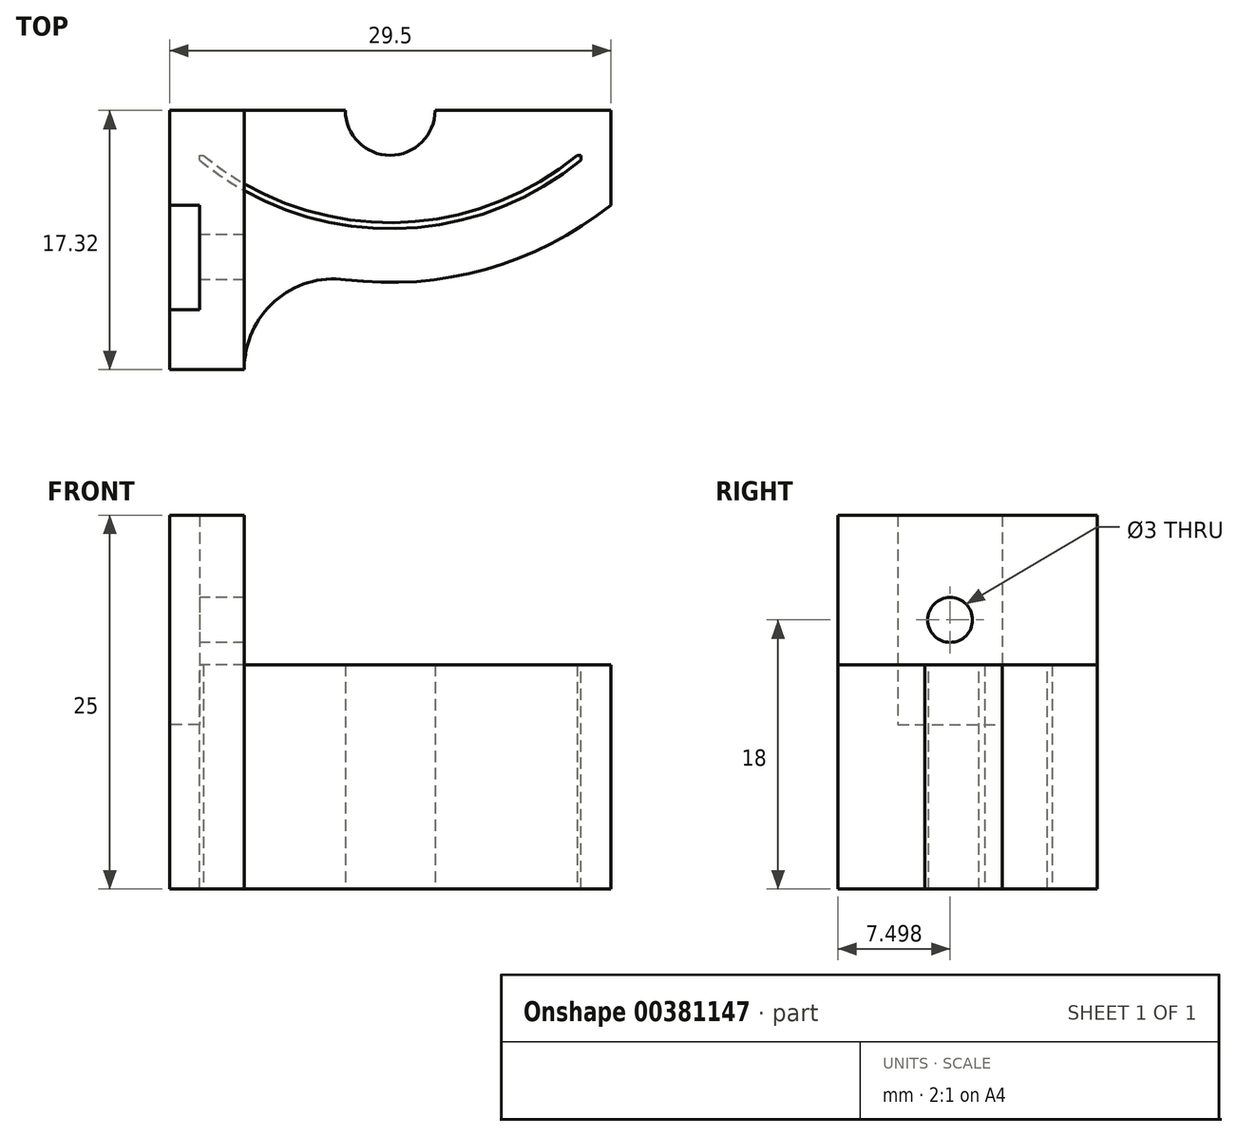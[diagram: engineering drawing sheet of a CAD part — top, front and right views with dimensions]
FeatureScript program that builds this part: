
annotation { "Feature Type Name" : "Feature", "Feature Type Description" : "" }
export const myFeature = defineFeature(function(context is Context, id is Id, definition is map)
    precondition{}
    {
        {
            var Q0;
            Q0=qCreatedBy(makeId("Top.planeOp"),FACE);
            var sketch = newSketch(context, id + "F0", { "sketchPlane" : qUnion([Q0])});
            skLineSegment(sketch, "E0", {"start": v(0, 0) * mm, "end": v(25, 0) * mm});
            skArc(sketch, "E1", {"start": v(0, 0) * mm, "mid": v(12.5, -4.5) * mm, "end": v(25, 0) * mm});
            skLineSegment(sketch, "E2.top", {"start": v(0, 3) * mm, "end": v(25, 3) * mm});
            skLineSegment(sketch, "E2.left", {"start": v(0, 0) * mm, "end": v(0, 3) * mm});
            skLineSegment(sketch, "E2.right", {"start": v(25, 0) * mm, "end": v(25, 3) * mm});
            skSolve(sketch);
        }
        {
            var Q0;
            Q0=makeQuery(id+"F0.imprint","IMPRINT",FACE,{"disambiguationData":[TD([[makeQuery(id+"F0.imprint","IMPRINT",EDGE,{"derivedFrom":sQuery(id+"F0.wireOp",EDGE,"E0")}),1.0]])]});
            var Q1;
            Q1=makeQuery(id+"F0.imprint","IMPRINT",FACE,{"disambiguationData":[TD([[makeQuery(id+"F0.imprint","IMPRINT",EDGE,{"derivedFrom":sQuery(id+"F0.wireOp",EDGE,"E1")}),1.0]])]});
            extrude(context, id + "F1", {"entities" : qUnion([Q0, Q1]), "depth" : 25 * mm});
        }
        {
            var Q0;
            Q0=makeQuery(id+"F1.opExtrude","CAP_FACE",FACE,{"disambiguationData":[OSD([sQuery(id+"F0.wireOp",EDGE,"E1"),sQuery(id+"F0.wireOp",EDGE,"E2.top"),sQuery(id+"F0.wireOp",EDGE,"E2.left"),sQuery(id+"F0.wireOp",EDGE,"E2.right")])],"isStart":false});
            var sketch = newSketch(context, id + "F2", { "sketchPlane" : qUnion([Q0])});
            skArc(sketch, "E3.0", {"start": v(-0.25, -0.3) * mm, "mid": v(12.5, -4.9) * mm, "end": v(25.25, -0.3) * mm});
            skLineSegment(sketch, "E4", {"start": v(-0.25, -0.3) * mm, "end": v(-2.25, -0.3) * mm});
            skLineSegment(sketch, "E5", {"start": v(-2.25, -0.3) * mm, "end": v(-2.25, 3) * mm});
            skLineSegment(sketch, "E6", {"start": v(0, 3) * mm, "end": v(-2.25, 3) * mm});
            skLineSegment(sketch, "E7", {"start": v(-0.25, -0.3) * mm, "end": v(-0.25, 0) * mm});
            skLineSegment(sketch, "E8", {"start": v(-0.25, 0) * mm, "end": v(0, 0) * mm});
            skArc(sketch, "E9.0", {"start": v(-2.25, -3.32) * mm, "mid": v(12.5, -8.5) * mm, "end": v(27.25, -3.32) * mm});
            skLineSegment(sketch, "E10", {"start": v(-2.25, -0.3) * mm, "end": v(-2.25, -3.32) * mm});
            skLineSegment(sketch, "E11.MirrorCS", {"start": v(25.25, 0) * mm, "end": v(25, 0) * mm});
            skLineSegment(sketch, "E12.MirrorCS", {"start": v(25.25, -0.3) * mm, "end": v(25.25, 0) * mm});
            skLineSegment(sketch, "E13.MirrorCS", {"start": v(25.25, -0.3) * mm, "end": v(27.25, -0.3) * mm});
            skLineSegment(sketch, "E14.MirrorCS", {"start": v(27.25, -0.3) * mm, "end": v(27.25, 3) * mm});
            skLineSegment(sketch, "E15.MirrorCS", {"start": v(27.25, -0.3) * mm, "end": v(27.25, -3.32) * mm});
            skLineSegment(sketch, "E16.MirrorCS", {"start": v(25, 3) * mm, "end": v(27.25, 3) * mm});
            skSolve(sketch);
        }
        {
            var Q0;
            Q0=makeQuery(id+"F2.imprint","IMPRINT",FACE,{"disambiguationData":[TD([[makeQuery(id+"F2.imprint","IMPRINT",EDGE,{"derivedFrom":sQuery(id+"F2.wireOp",EDGE,"E4")}),-1.0]])]});
            var Q1;
            Q1=makeQuery(id+"F2.imprint","IMPRINT",FACE,{"disambiguationData":[TD([[makeQuery(id+"F2.imprint","IMPRINT",EDGE,{"derivedFrom":sQuery(id+"F2.wireOp",EDGE,"E3.0")}),-1.0]])]});
            var Q2;
            Q2=makeQuery(id+"F2.imprint","IMPRINT",FACE,{"disambiguationData":[TD([[makeQuery(id+"F2.imprint","IMPRINT",EDGE,{"derivedFrom":sQuery(id+"F2.wireOp",EDGE,"E11.MirrorCS")}),-1.0]])]});
            extrude(context, id + "F3", {"entities" : qUnion([Q0, Q1, Q2]), "oppositeDirection" : true, "depth" : 25 * mm});
        }
        {
            var Q0;
            Q0=makeQuery(id+"F3.opExtrude","SWEPT_BODY",BODY,{"disambiguationData":[OSD([sQuery(id+"F0.wireOp",EDGE,"E2.left"),sQuery(id+"F0.wireOp",EDGE,"E2.right"),sQuery(id+"F2.wireOp",EDGE,"E3.0"),sQuery(id+"F2.wireOp",EDGE,"E5"),sQuery(id+"F2.wireOp",EDGE,"E6"),sQuery(id+"F2.wireOp",EDGE,"E7"),sQuery(id+"F2.wireOp",EDGE,"E8"),sQuery(id+"F2.wireOp",EDGE,"E9.0"),sQuery(id+"F2.wireOp",EDGE,"E10"),sQuery(id+"F2.wireOp",EDGE,"E11.MirrorCS"),sQuery(id+"F2.wireOp",EDGE,"E12.MirrorCS"),sQuery(id+"F2.wireOp",EDGE,"E14.MirrorCS"),sQuery(id+"F2.wireOp",EDGE,"E15.MirrorCS"),sQuery(id+"F2.wireOp",EDGE,"E16.MirrorCS")])]});
            var Q1;
            Q1=makeQuery(id+"F1.opExtrude","SWEPT_BODY",BODY,{"disambiguationData":[OSD([sQuery(id+"F0.wireOp",EDGE,"E1"),sQuery(id+"F0.wireOp",EDGE,"E2.top"),sQuery(id+"F0.wireOp",EDGE,"E2.left"),sQuery(id+"F0.wireOp",EDGE,"E2.right")])]});
            booleanBodies(context, id + "F4", {"operationType" : BooleanOperationType.UNION, "tools" : qUnion([Q0, Q1])});
        }
        {
            var Q0;
            {var subQ0=sQuery(id+"F0.wireOp",EDGE,"E2.right");var subQ1=sQuery(id+"F0.wireOp",EDGE,"E2.left");Q0=makeQuery(id+"F4.opBoolean","MERGE",FACE,{"derivedFrom":[makeQuery(id+"F1.opExtrude","CAP_FACE",FACE,{"disambiguationData":[OSD([sQuery(id+"F0.wireOp",EDGE,"E1"),sQuery(id+"F0.wireOp",EDGE,"E2.top"),subQ1,subQ0])],"isStart":true}),makeQuery(id+"F3.opExtrude","CAP_FACE",FACE,{"disambiguationData":[OSD([subQ1,subQ0,sQuery(id+"F2.wireOp",EDGE,"E3.0"),sQuery(id+"F2.wireOp",EDGE,"E5"),sQuery(id+"F2.wireOp",EDGE,"E6"),sQuery(id+"F2.wireOp",EDGE,"E7"),sQuery(id+"F2.wireOp",EDGE,"E8"),sQuery(id+"F2.wireOp",EDGE,"E9.0"),sQuery(id+"F2.wireOp",EDGE,"E10"),sQuery(id+"F2.wireOp",EDGE,"E11.MirrorCS"),sQuery(id+"F2.wireOp",EDGE,"E12.MirrorCS"),sQuery(id+"F2.wireOp",EDGE,"E14.MirrorCS"),sQuery(id+"F2.wireOp",EDGE,"E15.MirrorCS"),sQuery(id+"F2.wireOp",EDGE,"E16.MirrorCS")])],"isStart":false})]});}
            var sketch = newSketch(context, id + "F5", { "sketchPlane" : qUnion([Q0])});
            skLineSegment(sketch, "E17", {"start": v(12.5, -3) * mm, "end": v(12.5, 0) * mm});
            skLineSegment(sketch, "E18.0", {"start": v(15.5, -3) * mm, "end": v(18.5, -3) * mm});
            skLineSegment(sketch, "E19.0", {"start": v(9.5, -3) * mm, "end": v(6.5, -3) * mm});
            skArc(sketch, "E20", {"start": v(15.5, -3) * mm, "mid": v(12.5, 0) * mm, "end": v(9.5, -3) * mm});
            skLineSegment(sketch, "E21", {"start": v(15.5, -3) * mm, "end": v(9.5, -3) * mm});
            skSolve(sketch);
        }
        {
            var Q0;
            {var subQ0=sQuery(id+"F5.wireOp",EDGE,"E17");Q0=makeQuery(id+"F5.imprint","IMPRINT",FACE,{"disambiguationData":[TD([[makeQuery(id+"F5.imprint","IMPRINT",EDGE,{"derivedFrom":subQ0}),-1.0]])]});}
            var Q1;
            {var subQ0=sQuery(id+"F5.wireOp",EDGE,"E17");Q1=makeQuery(id+"F5.imprint","IMPRINT",FACE,{"disambiguationData":[TD([[makeQuery(id+"F5.imprint","IMPRINT",EDGE,{"derivedFrom":subQ0}),1.0]])]});}
            extrude(context, id + "F6", {"entities" : qUnion([Q0, Q1]), "operationType" : NewBodyOperationType.REMOVE, "oppositeDirection" : true, "depth" : 25 * mm});
        }
        {
            var Q0;
            Q0=makeQuery(id+"F3.opExtrude","SWEPT_FACE",FACE,{"disambiguationData":[OSD([sQuery(id+"F2.wireOp",EDGE,"E5"),sQuery(id+"F2.wireOp",EDGE,"E10")])]});
            var sketch = newSketch(context, id + "F7", { "sketchPlane" : qUnion([Q0])});
            skLineSegment(sketch, "E22.bottom", {"start": v(3.32, 25) * mm, "end": v(14.32, 25) * mm});
            skLineSegment(sketch, "E22.top", {"start": v(3.32, 0) * mm, "end": v(14.32, 0) * mm});
            skLineSegment(sketch, "E22.left", {"start": v(3.32, 25) * mm, "end": v(3.32, 0) * mm});
            skLineSegment(sketch, "E22.right", {"start": v(14.32, 25) * mm, "end": v(14.32, 0) * mm});
            skSolve(sketch);
        }
        {
            var Q0;
            Q0=makeQuery(id+"F7.imprint","IMPRINT",FACE,{"disambiguationData":[TD([[makeQuery(id+"F7.imprint","IMPRINT",EDGE,{"derivedFrom":sQuery(id+"F7.wireOp",EDGE,"E22.bottom")}),-1.0]])]});
            extrude(context, id + "F8", {"entities" : qUnion([Q0]), "oppositeDirection" : true, "depth" : 5 * mm});
        }
        {
            var Q0;
            Q0=makeQuery(id+"F8.opExtrude","CAP_FACE",FACE,{"disambiguationData":[OSD([sQuery(id+"F7.wireOp",EDGE,"E22.bottom"),sQuery(id+"F7.wireOp",EDGE,"E22.top"),sQuery(id+"F7.wireOp",EDGE,"E22.left"),sQuery(id+"F7.wireOp",EDGE,"E22.right")])],"isStart":true});
            var sketch = newSketch(context, id + "F9", { "sketchPlane" : qUnion([Q0])});
            skCircle(sketch, "E23", {"center": v(6.82, 18) * mm, "radius": 1.5 * mm});
            skLineSegment(sketch, "E24.bottom", {"start": v(3.32, 25) * mm, "end": v(10.32, 25) * mm});
            skLineSegment(sketch, "E24.top", {"start": v(3.32, 11) * mm, "end": v(10.32, 11) * mm});
            skLineSegment(sketch, "E24.left", {"start": v(3.32, 25) * mm, "end": v(3.32, 11) * mm});
            skLineSegment(sketch, "E24.right", {"start": v(10.32, 25) * mm, "end": v(10.32, 11) * mm});
            skSolve(sketch);
        }
        {
            var Q0;
            Q0=makeQuery(id+"F9.imprint","IMPRINT",FACE,{"disambiguationData":[TD([[makeQuery(id+"F9.imprint","IMPRINT",EDGE,{"derivedFrom":sQuery(id+"F9.wireOp",EDGE,"E23")}),1.0]])]});
            extrude(context, id + "F10", {"entities" : qUnion([Q0]), "operationType" : NewBodyOperationType.REMOVE, "oppositeDirection" : true, "depth" : 39.8 * mm});
        }
        {
            var Q0;
            Q0=makeQuery(id+"F8.opExtrude","CAP_FACE",FACE,{"disambiguationData":[OSD([sQuery(id+"F7.wireOp",EDGE,"E22.bottom"),sQuery(id+"F7.wireOp",EDGE,"E22.top"),sQuery(id+"F7.wireOp",EDGE,"E22.left"),sQuery(id+"F7.wireOp",EDGE,"E22.right")])],"isStart":false});
            var sketch = newSketch(context, id + "F11", { "sketchPlane" : qUnion([Q0])});
            skCircle(sketch, "E25", {"center": v(-6.82, 18) * mm, "radius": 2.5 * mm});
            skSolve(sketch);
        }
        {
            var Q0;
            Q0=makeQuery(id+"F11.imprint","IMPRINT",FACE,{"disambiguationData":[TD([[makeQuery(id+"F11.imprint","IMPRINT",EDGE,{"derivedFrom":sQuery(id+"F11.wireOp",EDGE,"E25")}),1.0]])]});
            extrude(context, id + "F12", {"entities" : qUnion([Q0]), "operationType" : NewBodyOperationType.REMOVE, "depth" : 25 * mm});
        }
        {
            var Q0;
            Q0=makeQuery(id+"F3.opExtrude","SWEPT_BODY",BODY,{"disambiguationData":[OSD([sQuery(id+"F0.wireOp",EDGE,"E2.left"),sQuery(id+"F0.wireOp",EDGE,"E2.right"),sQuery(id+"F2.wireOp",EDGE,"E3.0"),sQuery(id+"F2.wireOp",EDGE,"E5"),sQuery(id+"F2.wireOp",EDGE,"E6"),sQuery(id+"F2.wireOp",EDGE,"E7"),sQuery(id+"F2.wireOp",EDGE,"E8"),sQuery(id+"F2.wireOp",EDGE,"E9.0"),sQuery(id+"F2.wireOp",EDGE,"E10"),sQuery(id+"F2.wireOp",EDGE,"E11.MirrorCS"),sQuery(id+"F2.wireOp",EDGE,"E12.MirrorCS"),sQuery(id+"F2.wireOp",EDGE,"E14.MirrorCS"),sQuery(id+"F2.wireOp",EDGE,"E15.MirrorCS"),sQuery(id+"F2.wireOp",EDGE,"E16.MirrorCS")])]});
            var Q1;
            Q1=makeQuery(id+"F8.opExtrude","SWEPT_BODY",BODY,{"disambiguationData":[OSD([sQuery(id+"F7.wireOp",EDGE,"E22.bottom"),sQuery(id+"F7.wireOp",EDGE,"E22.top"),sQuery(id+"F7.wireOp",EDGE,"E22.left"),sQuery(id+"F7.wireOp",EDGE,"E22.right")])]});
            booleanBodies(context, id + "F13", {"operationType" : BooleanOperationType.UNION, "tools" : qUnion([Q0, Q1])});
        }
        {
            var Q0;
            Q0=makeQuery(id+"F13.opBoolean","MERGE",FACE,{"derivedFrom":[makeQuery(id+"F3.opExtrude","SWEPT_FACE",FACE,{"disambiguationData":[OSD([sQuery(id+"F2.wireOp",EDGE,"E5"),sQuery(id+"F2.wireOp",EDGE,"E10")])]}),makeQuery(id+"F8.opExtrude","CAP_FACE",FACE,{"disambiguationData":[OSD([sQuery(id+"F7.wireOp",EDGE,"E22.bottom"),sQuery(id+"F7.wireOp",EDGE,"E22.top"),sQuery(id+"F7.wireOp",EDGE,"E22.left"),sQuery(id+"F7.wireOp",EDGE,"E22.right")])],"isStart":true})]});
            var sketch = newSketch(context, id + "F14", { "sketchPlane" : qUnion([Q0])});
            skLineSegment(sketch, "E26", {"start": v(6.82, 18) * mm, "end": v(3.32, 18) * mm});
            skLineSegment(sketch, "E27", {"start": v(6.82, 18) * mm, "end": v(10.32, 18) * mm});
            skLineSegment(sketch, "E28.bottom", {"start": v(10.32, 18) * mm, "end": v(3.32, 18) * mm});
            skLineSegment(sketch, "E28.top", {"start": v(10.32, 11) * mm, "end": v(3.32, 11) * mm});
            skLineSegment(sketch, "E28.left", {"start": v(10.32, 18) * mm, "end": v(10.32, 11) * mm});
            skLineSegment(sketch, "E28.right", {"start": v(3.32, 18) * mm, "end": v(3.32, 11) * mm});
            skLineSegment(sketch, "E29.bottom", {"start": v(3.32, 18) * mm, "end": v(10.32, 18) * mm});
            skLineSegment(sketch, "E29.top", {"start": v(3.32, 25) * mm, "end": v(10.32, 25) * mm});
            skLineSegment(sketch, "E29.left", {"start": v(3.32, 18) * mm, "end": v(3.32, 25) * mm});
            skLineSegment(sketch, "E29.right", {"start": v(10.32, 18) * mm, "end": v(10.32, 25) * mm});
            skSolve(sketch);
        }
        {
            var Q0;
            Q0=makeQuery(id+"F14.imprint","IMPRINT",FACE,{"disambiguationData":[TD([[makeQuery(id+"F14.imprint","IMPRINT",EDGE,{"derivedFrom":sQuery(id+"F14.wireOp",EDGE,"E28.top")}),-1.0]])]});
            var Q1;
            Q1=makeQuery(id+"F14.imprint","IMPRINT",FACE,{"disambiguationData":[TD([[makeQuery(id+"F14.imprint","IMPRINT",EDGE,{"derivedFrom":sQuery(id+"F14.wireOp",EDGE,"E29.top")}),1.0]])]});
            extrude(context, id + "F15", {"entities" : qUnion([Q0, Q1]), "operationType" : NewBodyOperationType.REMOVE, "oppositeDirection" : true, "depth" : 2 * mm});
        }
        {
            var Q0;
            {var subQ0=sQuery(id+"F0.wireOp",EDGE,"E2.right");var subQ1=sQuery(id+"F0.wireOp",EDGE,"E2.left");Q0=makeQuery(id+"F13.opBoolean","MERGE",FACE,{"derivedFrom":[makeQuery(id+"F4.opBoolean","MERGE",FACE,{"derivedFrom":[makeQuery(id+"F1.opExtrude","CAP_FACE",FACE,{"disambiguationData":[OSD([sQuery(id+"F0.wireOp",EDGE,"E1"),sQuery(id+"F0.wireOp",EDGE,"E2.top"),subQ1,subQ0])],"isStart":false}),makeQuery(id+"F3.opExtrude","CAP_FACE",FACE,{"disambiguationData":[OSD([subQ1,subQ0,sQuery(id+"F2.wireOp",EDGE,"E3.0"),sQuery(id+"F2.wireOp",EDGE,"E5"),sQuery(id+"F2.wireOp",EDGE,"E6"),sQuery(id+"F2.wireOp",EDGE,"E7"),sQuery(id+"F2.wireOp",EDGE,"E8"),sQuery(id+"F2.wireOp",EDGE,"E9.0"),sQuery(id+"F2.wireOp",EDGE,"E10"),sQuery(id+"F2.wireOp",EDGE,"E11.MirrorCS"),sQuery(id+"F2.wireOp",EDGE,"E12.MirrorCS"),sQuery(id+"F2.wireOp",EDGE,"E14.MirrorCS"),sQuery(id+"F2.wireOp",EDGE,"E15.MirrorCS"),sQuery(id+"F2.wireOp",EDGE,"E16.MirrorCS")])],"isStart":true})]}),makeQuery(id+"F8.opExtrude","SWEPT_FACE",FACE,{"disambiguationData":[OSD([sQuery(id+"F7.wireOp",EDGE,"E22.bottom")])]})]});}
            var sketch = newSketch(context, id + "F16", { "sketchPlane" : qUnion([Q0])});
            skLineSegment(sketch, "E30.bottom", {"start": v(2.75, -14.32) * mm, "end": v(43.61, -14.32) * mm});
            skLineSegment(sketch, "E30.top", {"start": v(2.75, 7.64) * mm, "end": v(43.61, 7.64) * mm});
            skLineSegment(sketch, "E30.left", {"start": v(2.75, -14.32) * mm, "end": v(2.75, 7.64) * mm});
            skLineSegment(sketch, "E30.right", {"start": v(43.61, -14.32) * mm, "end": v(43.61, 7.64) * mm});
            skSolve(sketch);
        }
        {
            var Q0;
            {var subQ1=sQuery(id+"F16.wireOp",EDGE,"E30.bottom");Q0=makeQuery(id+"F16.imprint","IMPRINT",FACE,{"disambiguationData":[TD([[makeQuery(id+"F16.imprint","IMPRINT",EDGE,{"derivedFrom":subQ1}),1.0]])]});}
            var Q1;
            {var subQ11=sQuery(id+"F2.wireOp",EDGE,"E11.MirrorCS");var subQ27=makeQuery(id+"F3.opExtrude","CAP_EDGE",EDGE,{"disambiguationData":[OSD([subQ11])],"isStart":true});Q1=makeQuery(id+"F16.imprint","IMPRINT",FACE,{"disambiguationData":[TD([[makeQuery(id+"F16.imprint","IMPRINT",EDGE,{"derivedFrom":subQ27}),-1.0]])]});}
            extrude(context, id + "F17", {"entities" : qUnion([Q0, Q1]), "operationType" : NewBodyOperationType.REMOVE, "oppositeDirection" : true, "depth" : 10 * mm});
        }
        {
            var Q0;
            Q0=makeQuery(id+"F13.opBoolean","INTERSECT",EDGE,{"disambiguationData":[OD(0.0)],"derivedFrom":[makeQuery(id+"F3.opExtrude","SWEPT_FACE",FACE,{"disambiguationData":[OSD([sQuery(id+"F2.wireOp",EDGE,"E9.0")])]}),makeQuery(id+"F8.opExtrude","CAP_FACE",FACE,{"disambiguationData":[OSD([sQuery(id+"F7.wireOp",EDGE,"E22.bottom"),sQuery(id+"F7.wireOp",EDGE,"E22.top"),sQuery(id+"F7.wireOp",EDGE,"E22.left"),sQuery(id+"F7.wireOp",EDGE,"E22.right")])],"isStart":false})]});
            fillet(context, id + "F18", {"entities" : qUnion([Q0]), "radius" : 6 * mm, "tangentPropagation" : true, "allowEdgeOverflow" : false});
        }
        {
            var Q0;
            {var subQ0=sQuery(id+"F16.wireOp",EDGE,"E30.left");var subQ8=sQuery(id+"F0.wireOp",EDGE,"E1");Q0=makeQuery(id+"F17.boolean.opBoolean","COPY",FACE,{"derivedFrom":makeQuery(id+"F17.opExtrude","SWEPT_FACE",FACE,{"disambiguationData":[OSD([subQ0]),TDD([makeQuery(id+"F16.imprint","IMPRINT",EDGE,{"disambiguationData":[TD([[makeQuery(id+"F16.imprint","INTERSECT",VERTEX,{"derivedFrom":[makeQuery(id+"F1.opExtrude","CAP_EDGE",EDGE,{"disambiguationData":[OSD([subQ8])],"isStart":false}),subQ0]}),-1.0]])],"derivedFrom":subQ0}),makeQuery(id+"F16.imprint","IMPRINT",EDGE,{"disambiguationData":[TD([[makeQuery(id+"F16.imprint","INTERSECT",VERTEX,{"derivedFrom":[sQuery(id+"F16.wireOp",EDGE,"E30.top"),subQ0]}),1.0]])],"derivedFrom":subQ0})])]})});}
            var sketch = newSketch(context, id + "F19", { "sketchPlane" : qUnion([Q0])});
            skPoint(sketch, "E31.0", {"position": v(-3.32, 25) * mm});
            skLineSegment(sketch, "E32.bottom", {"start": v(-3.32, 25) * mm, "end": v(3, 25) * mm});
            skLineSegment(sketch, "E32.top", {"start": v(-3.32, 15) * mm, "end": v(3, 15) * mm});
            skLineSegment(sketch, "E32.left", {"start": v(-3.32, 25) * mm, "end": v(-3.32, 15) * mm});
            skLineSegment(sketch, "E32.right", {"start": v(3, 25) * mm, "end": v(3, 15) * mm});
            skSolve(sketch);
        }
        {
            var Q0;
            {var subQ2=sQuery(id+"F19.wireOp",EDGE,"E32.right");Q0=makeQuery(id+"F19.imprint","IMPRINT",FACE,{"disambiguationData":[TD([[makeQuery(id+"F19.imprint","IMPRINT",EDGE,{"derivedFrom":subQ2}),1.0]])]});}
            var Q1;
            {var subQ2=sQuery(id+"F19.wireOp",EDGE,"E32.left");Q1=makeQuery(id+"F19.imprint","IMPRINT",FACE,{"disambiguationData":[TD([[makeQuery(id+"F19.imprint","IMPRINT",EDGE,{"derivedFrom":subQ2}),1.0]])]});}
            var Q2;
            Q2=makeQuery(id+"F13.opBoolean","MERGE",FACE,{"derivedFrom":[makeQuery(id+"F3.opExtrude","SWEPT_FACE",FACE,{"disambiguationData":[OSD([sQuery(id+"F2.wireOp",EDGE,"E5"),sQuery(id+"F2.wireOp",EDGE,"E10")])]}),makeQuery(id+"F8.opExtrude","CAP_FACE",FACE,{"disambiguationData":[OSD([sQuery(id+"F7.wireOp",EDGE,"E22.bottom"),sQuery(id+"F7.wireOp",EDGE,"E22.top"),sQuery(id+"F7.wireOp",EDGE,"E22.left"),sQuery(id+"F7.wireOp",EDGE,"E22.right")])],"isStart":true})]});
            extrude(context, id + "F20", {"entities" : qUnion([Q0, Q1]), "operationType" : NewBodyOperationType.ADD, "endBound" : BoundingType.UP_TO_SURFACE, "oppositeDirection" : true, "endBoundEntityFace" : qUnion([Q2]), "depth" : 25 * mm});
        }
    });
